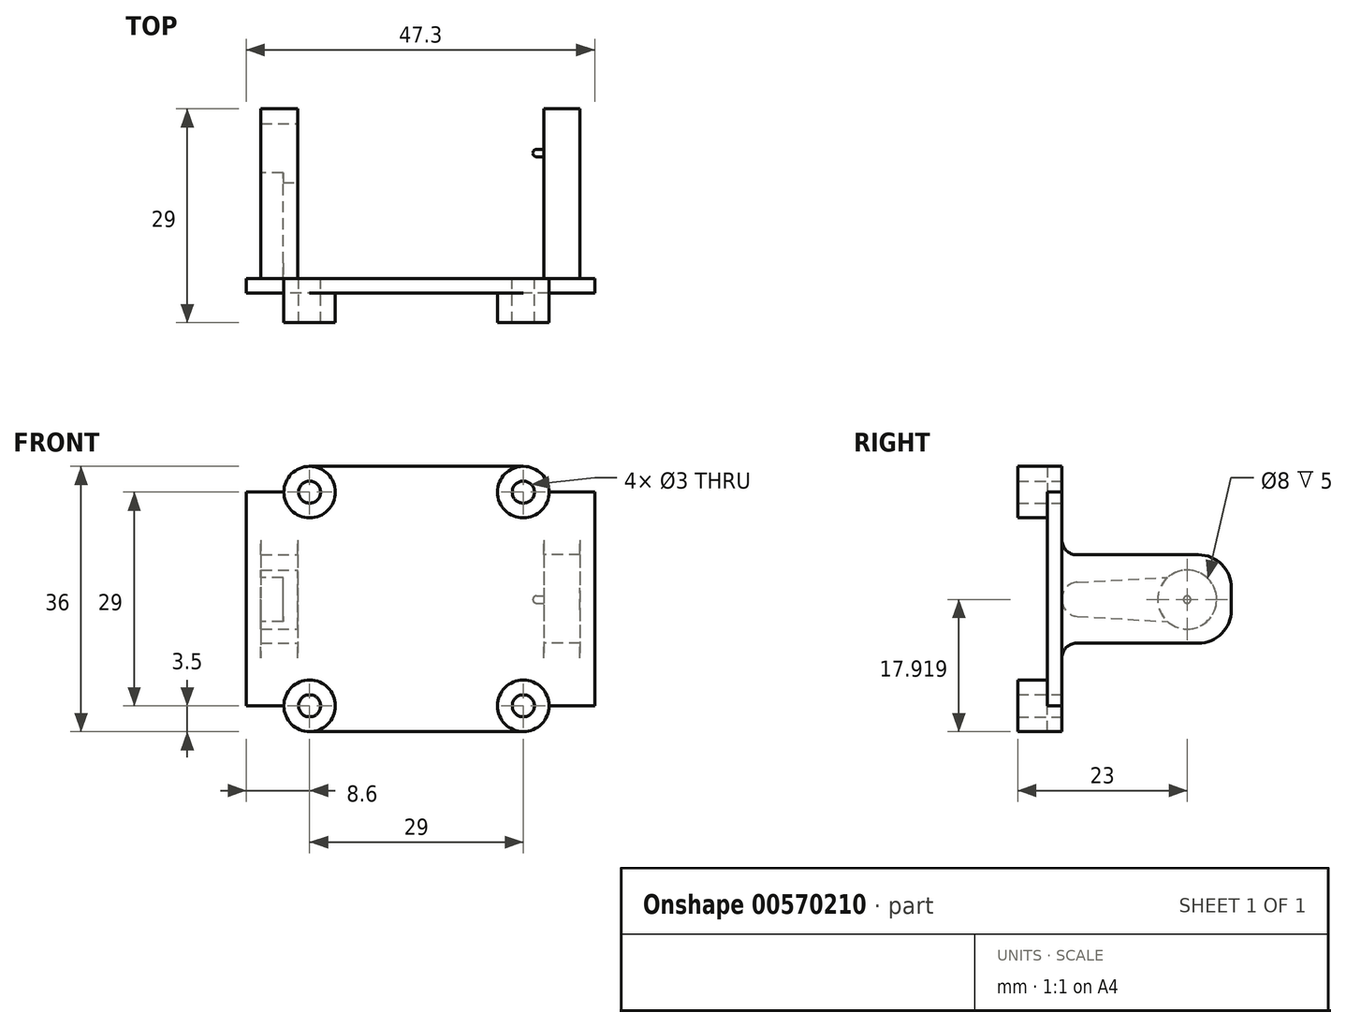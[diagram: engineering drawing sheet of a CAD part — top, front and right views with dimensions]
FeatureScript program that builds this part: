
annotation { "Feature Type Name" : "Feature", "Feature Type Description" : "" }
export const myFeature = defineFeature(function(context is Context, id is Id, definition is map)
    precondition{}
    {
        {
            var Q0;
            Q0=qCreatedBy(makeId("Front.planeOp"),FACE);
            var sketch = newSketch(context, id + "F0", { "sketchPlane" : qUnion([Q0])});
            skLineSegment(sketch, "E0.bottom", {"start": v(0, 0) * mm, "end": v(36, 0) * mm});
            skLineSegment(sketch, "E0.top", {"start": v(0, 36) * mm, "end": v(36, 36) * mm});
            skLineSegment(sketch, "E0.left", {"start": v(0, 0) * mm, "end": v(0, 36) * mm});
            skLineSegment(sketch, "E0.right", {"start": v(36, 0) * mm, "end": v(36, 36) * mm});
            skSolve(sketch);
        }
        {
            var Q0;
            Q0=makeQuery(id+"F0.imprint","IMPRINT",FACE,{"disambiguationData":[TD([[makeQuery(id+"F0.imprint","IMPRINT",EDGE,{"derivedFrom":sQuery(id+"F0.wireOp",EDGE,"E0.bottom")}),1.0]])]});
            extrude(context, id + "F1", {"entities" : qUnion([Q0]), "depth" : 2 * mm, "offsetDistance" : 25 * mm});
        }
        {
            var Q0;
            Q0=makeQuery(id+"F1.opExtrude","CAP_FACE",FACE,{"disambiguationData":[OSD([sQuery(id+"F0.wireOp",EDGE,"E0.bottom"),sQuery(id+"F0.wireOp",EDGE,"E0.top"),sQuery(id+"F0.wireOp",EDGE,"E0.left"),sQuery(id+"F0.wireOp",EDGE,"E0.right")])],"isStart":false});
            var sketch = newSketch(context, id + "F2", { "sketchPlane" : qUnion([Q0])});
            skCircle(sketch, "E1", {"center": v(3.5, 32.5) * mm, "radius": 3.5 * mm});
            skCircle(sketch, "E2", {"center": v(32.5, 32.5) * mm, "radius": 3.5 * mm});
            skCircle(sketch, "E3", {"center": v(32.5, 3.5) * mm, "radius": 3.5 * mm});
            skCircle(sketch, "E4", {"center": v(3.5, 3.5) * mm, "radius": 3.5 * mm});
            skCircle(sketch, "E5", {"center": v(3.5, 32.5) * mm, "radius": 1.5 * mm});
            skCircle(sketch, "E6", {"center": v(32.5, 32.5) * mm, "radius": 1.5 * mm});
            skCircle(sketch, "E7", {"center": v(32.5, 3.5) * mm, "radius": 1.5 * mm});
            skCircle(sketch, "E8", {"center": v(3.5, 3.5) * mm, "radius": 1.5 * mm});
            skSolve(sketch);
        }
        {
            var Q0;
            Q0=qSketchRegion(id+"F2",true);
            extrude(context, id + "F3", {"entities" : qUnion([Q0]), "operationType" : NewBodyOperationType.ADD, "depth" : 3 * mm, "offsetDistance" : 25 * mm});
        }
        {
            var Q0;
            Q0=makeQuery(id+"F1.opExtrude","SWEPT_EDGE",EDGE,{"disambiguationData":[OSD([sQuery(id+"F0.wireOp",EDGE,"E0.top"),sQuery(id+"F0.wireOp",EDGE,"E0.left")])]});
            var Q1;
            Q1=makeQuery(id+"F1.opExtrude","SWEPT_EDGE",EDGE,{"disambiguationData":[OSD([sQuery(id+"F0.wireOp",EDGE,"E0.top"),sQuery(id+"F0.wireOp",EDGE,"E0.right")])]});
            var Q2;
            Q2=makeQuery(id+"F1.opExtrude","SWEPT_EDGE",EDGE,{"disambiguationData":[OSD([sQuery(id+"F0.wireOp",EDGE,"E0.bottom"),sQuery(id+"F0.wireOp",EDGE,"E0.right")])]});
            var Q3;
            Q3=makeQuery(id+"F1.opExtrude","SWEPT_EDGE",EDGE,{"disambiguationData":[OSD([sQuery(id+"F0.wireOp",EDGE,"E0.bottom"),sQuery(id+"F0.wireOp",EDGE,"E0.left")])]});
            fillet(context, id + "F4", {"entities" : qUnion([Q0, Q1, Q2, Q3]), "radius" : 3.5 * mm, "tangentPropagation" : true, "allowEdgeOverflow" : false});
        }
        {
            var Q0;
            Q0=makeQuery(id+"F7.boolean.opBoolean","MERGE",FACE,{"derivedFrom":[makeQuery(id+"F1.opExtrude","SWEPT_FACE",FACE,{"disambiguationData":[OSD([sQuery(id+"F0.wireOp",EDGE,"E0.right")])]}),makeQuery(id+"F7.opExtrude","SWEPT_FACE",FACE,{"disambiguationData":[OSD([sQuery(id+"F6.wireOp",EDGE,"E11.left")])]})]});
            extrude(context, id + "F5", {"entities" : qUnion([Q0]), "operationType" : NewBodyOperationType.ADD, "depth" : 1.2 * mm, "offsetDistance" : 25 * mm});
        }
        {
            var Q0;
            Q0=makeQuery(id+"F1.opExtrude","CAP_FACE",FACE,{"disambiguationData":[OSD([sQuery(id+"F0.wireOp",EDGE,"E0.bottom"),sQuery(id+"F0.wireOp",EDGE,"E0.top"),sQuery(id+"F0.wireOp",EDGE,"E0.left"),sQuery(id+"F0.wireOp",EDGE,"E0.right")])],"isStart":true});
            var sketch = newSketch(context, id + "F6", { "sketchPlane" : qUnion([Q0])});
            skArc(sketch, "E9.0.1", {"start": v(0, 32.5) * mm, "mid": v(-1.03, 34.97) * mm, "end": v(-3.5, 36) * mm, "construction": true});
            skLineSegment(sketch, "E9.0.2", {"start": v(-3.5, 36) * mm, "end": v(-32.5, 36) * mm, "construction": true});
            skArc(sketch, "E9.0.3", {"start": v(-32.5, 36) * mm, "mid": v(-34.97, 34.97) * mm, "end": v(-36, 32.5) * mm, "construction": true});
            skArc(sketch, "E9.0.5", {"start": v(-36, 3.5) * mm, "mid": v(-34.97, 1.03) * mm, "end": v(-32.5, 0) * mm, "construction": true});
            skLineSegment(sketch, "E9.0.6", {"start": v(-32.5, 0) * mm, "end": v(-3.5, 0) * mm, "construction": true});
            skArc(sketch, "E9.0.7", {"start": v(-3.5, 0) * mm, "mid": v(-1.03, 1.03) * mm, "end": v(0, 3.5) * mm, "construction": true});
            skLineSegment(sketch, "E10.0", {"start": v(0, 3.5) * mm, "end": v(0, 32.5) * mm, "construction": true});
            skLineSegment(sketch, "E11.bottom", {"start": v(-37.2, 24) * mm, "end": v(-35.3, 24) * mm});
            skLineSegment(sketch, "E11.top", {"start": v(-37.2, 12) * mm, "end": v(-35.3, 12) * mm});
            skLineSegment(sketch, "E11.left", {"start": v(-37.2, 24) * mm, "end": v(-37.2, 12) * mm});
            skLineSegment(sketch, "E11.right", {"start": v(-35.3, 24) * mm, "end": v(-35.3, 12) * mm});
            skLineSegment(sketch, "E12.bottom", {"start": v(0, 24) * mm, "end": v(-1.9, 24) * mm});
            skLineSegment(sketch, "E12.top", {"start": v(0, 12) * mm, "end": v(-1.9, 12) * mm});
            skLineSegment(sketch, "E12.left", {"start": v(0, 24) * mm, "end": v(0, 12) * mm});
            skLineSegment(sketch, "E12.right", {"start": v(-1.9, 24) * mm, "end": v(-1.9, 12) * mm});
            skPoint(sketch, "E13", {"position": v(-1.9, 18) * mm});
            skPoint(sketch, "E14", {"position": v(0, 18) * mm});
            skLineSegment(sketch, "E15.0", {"start": v(-37.2, 3.5) * mm, "end": v(-37.2, 32.5) * mm, "construction": true});
            skSolve(sketch);
        }
        {
            var Q0;
            Q0=makeQuery(id+"F6.imprint","IMPRINT",FACE,{"disambiguationData":[TD([[makeQuery(id+"F6.imprint","IMPRINT",EDGE,{"derivedFrom":sQuery(id+"F6.wireOp",EDGE,"E11.bottom")}),-1.0]])]});
            var Q1;
            Q1=makeQuery(id+"F6.imprint","IMPRINT",FACE,{"disambiguationData":[TD([[makeQuery(id+"F6.imprint","IMPRINT",EDGE,{"derivedFrom":sQuery(id+"F6.wireOp",EDGE,"E12.bottom")}),1.0]])]});
            extrude(context, id + "F7", {"entities" : qUnion([Q0, Q1]), "operationType" : NewBodyOperationType.ADD, "depth" : 23 * mm, "offsetDistance" : 25 * mm});
        }
        {
            var Q0;
            Q0=makeQuery(id+"F7.boolean.opBoolean","MERGE",FACE,{"derivedFrom":[makeQuery(id+"F1.opExtrude","SWEPT_FACE",FACE,{"disambiguationData":[OSD([sQuery(id+"F0.wireOp",EDGE,"E0.left")])]}),makeQuery(id+"F7.opExtrude","SWEPT_FACE",FACE,{"disambiguationData":[OSD([sQuery(id+"F6.wireOp",EDGE,"E12.left")])]})]});
            extrude(context, id + "F8", {"entities" : qUnion([Q0]), "operationType" : NewBodyOperationType.ADD, "depth" : 1.2 * mm, "offsetDistance" : 25 * mm});
        }
        {
            var Q0;
            Q0=makeQuery(id+"F7.opExtrude","SWEPT_FACE",FACE,{"disambiguationData":[OSD([sQuery(id+"F6.wireOp",EDGE,"E12.right")])]});
            var sketch = newSketch(context, id + "F9", { "sketchPlane" : qUnion([Q0])});
            skCircle(sketch, "E16", {"center": v(17, 17.92) * mm, "radius": 4 * mm});
            skSolve(sketch);
        }
        {
            var Q0;
            Q0=makeQuery(id+"F7.opExtrude","SWEPT_FACE",FACE,{"disambiguationData":[OSD([sQuery(id+"F6.wireOp",EDGE,"E11.right")])]});
            var sketch = newSketch(context, id + "F10", { "sketchPlane" : qUnion([Q0])});
            skCircle(sketch, "E17.0", {"center": v(-17, 17.92) * mm, "radius": 4 * mm, "construction": true});
            skCircle(sketch, "E18", {"center": v(-17, 17.92) * mm, "radius": 0.5 * mm});
            skSolve(sketch);
        }
        {
            var Q0;
            Q0 = qSketchRegion(id + "F10", true);
            extrude(context, id + "F11", {"entities" : qUnion([Q0]), "operationType" : NewBodyOperationType.ADD, "depth" : 1.5 * mm, "offsetDistance" : 25 * mm});
        }
        {
            var Q0;
            Q0=makeQuery(id+"F11.opExtrude","CAP_EDGE",EDGE,{"disambiguationData":[OSD([sQuery(id+"F10.wireOp",EDGE,"E18")])],"isStart":false});
            fillet(context, id + "F12", {"entities" : qUnion([Q0]), "radius" : .5 * mm, "tangentPropagation" : true, "allowEdgeOverflow" : false});
        }
        {
            var Q0;
            Q0 = qSketchRegion(id + "F9", true);
            extrude(context, id + "F13", {"entities" : qUnion([Q0]), "operationType" : NewBodyOperationType.REMOVE, "oppositeDirection" : true, "depth" : 2.5 * mm, "offsetDistance" : 25 * mm});
        }
        {
            var Q0;
            Q0=makeQuery(id+"F7.opExtrude","CAP_EDGE",EDGE,{"disambiguationData":[OSD([sQuery(id+"F6.wireOp",EDGE,"E11.bottom")])],"isStart":false});
            var Q1;
            Q1=makeQuery(id+"F7.opExtrude","CAP_EDGE",EDGE,{"disambiguationData":[OSD([sQuery(id+"F6.wireOp",EDGE,"E11.top")])],"isStart":false});
            var Q2;
            {var subQ0=sQuery(id+"F6.wireOp",EDGE,"E12.left");var subQ1=sQuery(id+"F6.wireOp",EDGE,"E12.top");var subQ2=sQuery(id+"F0.wireOp",EDGE,"E0.left");Q2=makeQuery(id+"F8.boolean.opBoolean","MERGE",EDGE,{"derivedFrom":[makeQuery(id+"F7.opExtrude","CAP_EDGE",EDGE,{"disambiguationData":[OSD([subQ1])],"isStart":false}),makeQuery(id+"F8.opExtrude","SWEPT_EDGE",EDGE,{"disambiguationData":[OSD([subQ2,subQ1,subQ0]),TDD([makeQuery(id+"F7.opExtrude","CAP_VERTEX",VERTEX,{"disambiguationData":[OSD([subQ2,subQ1,subQ0])],"isStart":false})])]})]});}
            var Q3;
            {var subQ0=sQuery(id+"F6.wireOp",EDGE,"E12.left");var subQ1=sQuery(id+"F6.wireOp",EDGE,"E12.bottom");var subQ2=sQuery(id+"F0.wireOp",EDGE,"E0.left");Q3=makeQuery(id+"F8.boolean.opBoolean","MERGE",EDGE,{"derivedFrom":[makeQuery(id+"F7.opExtrude","CAP_EDGE",EDGE,{"disambiguationData":[OSD([subQ1])],"isStart":false}),makeQuery(id+"F8.opExtrude","SWEPT_EDGE",EDGE,{"disambiguationData":[OSD([subQ2,subQ1,subQ0]),TDD([makeQuery(id+"F7.opExtrude","CAP_VERTEX",VERTEX,{"disambiguationData":[OSD([subQ2,subQ1,subQ0])],"isStart":false})])]})]});}
            fillet(context, id + "F14", {"entities" : qUnion([Q0, Q1, Q2, Q3]), "radius" : 4.5 * mm, "tangentPropagation" : true, "allowEdgeOverflow" : false});
        }
        {
            var Q0;
            Q0=makeQuery(id+"F8.opExtrude","CAP_FACE",FACE,{"disambiguationData":[OSD([sQuery(id+"F0.wireOp",EDGE,"E0.left"),sQuery(id+"F6.wireOp",EDGE,"E12.left")])],"isStart":false});
            var sketch = newSketch(context, id + "F15", { "sketchPlane" : qUnion([Q0])});
            skCircle(sketch, "E19.0.0", {"center": v(-17, 17.92) * mm, "radius": 4 * mm});
            skLineSegment(sketch, "E20.left", {"start": v(-14.35, 20.92) * mm, "end": v(-14.35, 17.92) * mm});
            skLineSegment(sketch, "E20.right", {"start": v(0, 18.08) * mm, "end": v(0, 17.84) * mm});
            skLineSegment(sketch, "E21", {"start": v(-14.35, 20.92) * mm, "end": v(-2.08, 20.27) * mm});
            skLineSegment(sketch, "E22", {"start": v(-14.35, 14.92) * mm, "end": v(-2.07, 15.64) * mm});
            skPoint(sketch, "E23", {"position": v(-14.35, 17.92) * mm});
            skPoint(sketch, "E24", {"position": v(0, 17.92) * mm});
            skPoint(sketch, "E25.visualSharp", {"position": v(0, 20.17) * mm});
            skArc(sketch, "E25.filletArc", {"start": v(0, 18.08) * mm, "mid": v(-0.6, 19.6) * mm, "end": v(-2.08, 20.27) * mm});
            skPoint(sketch, "E26.visualSharp", {"position": v(0, 15.77) * mm});
            skArc(sketch, "E26.filletArc", {"start": v(-2.07, 15.64) * mm, "mid": v(-0.6, 16.33) * mm, "end": v(0, 17.84) * mm});
            skSolve(sketch);
        }
        {
            var Q0;
            Q0 = qSketchRegion(id + "F15", true);
            var Q1;
            Q1=makeQuery(id+"F7.opExtrude","SWEPT_FACE",FACE,{"disambiguationData":[OSD([sQuery(id+"F6.wireOp",EDGE,"E12.right")])]});
            extrude(context, id + "F16", {"entities" : qUnion([Q0]), "operationType" : NewBodyOperationType.REMOVE, "endBound" : BoundingType.UP_TO_SURFACE, "oppositeDirection" : true, "depth" : 25 * mm, "endBoundEntityFace" : qUnion([Q1]), "hasOffset" : true, "offsetDistance" : 2 * mm});
        }
        {
            var Q0;
            Q0=makeQuery(id+"F3.boolean.opBoolean","SPLIT",FACE,{"disambiguationData":[TD([makeQuery(id+"F3.opExtrude","SWEPT_FACE",FACE,{"disambiguationData":[OSD([sQuery(id+"F2.wireOp",EDGE,"E6")])]})])],"derivedFrom":makeQuery(id+"F1.opExtrude","CAP_FACE",FACE,{"disambiguationData":[OSD([sQuery(id+"F0.wireOp",EDGE,"E0.bottom"),sQuery(id+"F0.wireOp",EDGE,"E0.top"),sQuery(id+"F0.wireOp",EDGE,"E0.left"),sQuery(id+"F0.wireOp",EDGE,"E0.right")])],"isStart":false})});
            var Q1;
            Q1=makeQuery(id+"F3.boolean.opBoolean","SPLIT",FACE,{"disambiguationData":[TD([makeQuery(id+"F3.opExtrude","SWEPT_FACE",FACE,{"disambiguationData":[OSD([sQuery(id+"F2.wireOp",EDGE,"E7")])]})])],"derivedFrom":makeQuery(id+"F1.opExtrude","CAP_FACE",FACE,{"disambiguationData":[OSD([sQuery(id+"F0.wireOp",EDGE,"E0.bottom"),sQuery(id+"F0.wireOp",EDGE,"E0.top"),sQuery(id+"F0.wireOp",EDGE,"E0.left"),sQuery(id+"F0.wireOp",EDGE,"E0.right")])],"isStart":false})});
            var Q2;
            Q2=makeQuery(id+"F3.boolean.opBoolean","SPLIT",FACE,{"disambiguationData":[TD([makeQuery(id+"F3.opExtrude","SWEPT_FACE",FACE,{"disambiguationData":[OSD([sQuery(id+"F2.wireOp",EDGE,"E8")])]})])],"derivedFrom":makeQuery(id+"F1.opExtrude","CAP_FACE",FACE,{"disambiguationData":[OSD([sQuery(id+"F0.wireOp",EDGE,"E0.bottom"),sQuery(id+"F0.wireOp",EDGE,"E0.top"),sQuery(id+"F0.wireOp",EDGE,"E0.left"),sQuery(id+"F0.wireOp",EDGE,"E0.right")])],"isStart":false})});
            var Q3;
            Q3=makeQuery(id+"F3.boolean.opBoolean","SPLIT",FACE,{"disambiguationData":[TD([makeQuery(id+"F3.opExtrude","SWEPT_FACE",FACE,{"disambiguationData":[OSD([sQuery(id+"F2.wireOp",EDGE,"E5")])]})])],"derivedFrom":makeQuery(id+"F1.opExtrude","CAP_FACE",FACE,{"disambiguationData":[OSD([sQuery(id+"F0.wireOp",EDGE,"E0.bottom"),sQuery(id+"F0.wireOp",EDGE,"E0.top"),sQuery(id+"F0.wireOp",EDGE,"E0.left"),sQuery(id+"F0.wireOp",EDGE,"E0.right")])],"isStart":false})});
            extrude(context, id + "F17", {"entities" : qUnion([Q0, Q1, Q2, Q3]), "operationType" : NewBodyOperationType.REMOVE, "endBound" : BoundingType.UP_TO_NEXT, "oppositeDirection" : true, "depth" : 25 * mm, "offsetDistance" : 25 * mm});
        }
        {
            var Q0;
            Q0=makeQuery(id+"F7.boolean.opBoolean","MERGE",FACE,{"derivedFrom":[makeQuery(id+"F5.opExtrude","CAP_FACE",FACE,{"disambiguationData":[OSD([sQuery(id+"F0.wireOp",EDGE,"E0.right")])],"isStart":false}),makeQuery(id+"F7.opExtrude","SWEPT_FACE",FACE,{"disambiguationData":[OSD([sQuery(id+"F6.wireOp",EDGE,"E11.left")])]})]});
            extrude(context, id + "F18", {"entities" : qUnion([Q0]), "operationType" : NewBodyOperationType.ADD, "depth" : 3 * mm, "offsetDistance" : 25 * mm});
        }
        {
            var Q0;
            Q0=makeQuery(id+"F8.opExtrude","CAP_FACE",FACE,{"disambiguationData":[OSD([sQuery(id+"F0.wireOp",EDGE,"E0.left"),sQuery(id+"F6.wireOp",EDGE,"E12.left")])],"isStart":false});
            extrude(context, id + "F19", {"entities" : qUnion([Q0]), "operationType" : NewBodyOperationType.ADD, "depth" : 1.9 * mm, "offsetDistance" : 25 * mm});
        }
        {
            var Q0;
            Q0=makeQuery(id+"F18.opExtrude","CAP_FACE",FACE,{"disambiguationData":[OSD([sQuery(id+"F0.wireOp",EDGE,"E0.right"),sQuery(id+"F6.wireOp",EDGE,"E11.left")])],"isStart":false});
            var sketch = newSketch(context, id + "F20", { "sketchPlane" : qUnion([Q0])});
            skLineSegment(sketch, "E27.bottom", {"start": v(-2, 32.5) * mm, "end": v(0, 32.5) * mm});
            skLineSegment(sketch, "E27.top", {"start": v(-2, 3.5) * mm, "end": v(0, 3.5) * mm});
            skLineSegment(sketch, "E27.left", {"start": v(-2, 32.5) * mm, "end": v(-2, 3.5) * mm});
            skLineSegment(sketch, "E27.right", {"start": v(0, 32.5) * mm, "end": v(0, 3.5) * mm});
            skSolve(sketch);
        }
        {
            var Q0;
            Q0 = qSketchRegion(id + "F20", true);
            extrude(context, id + "F21", {"entities" : qUnion([Q0]), "operationType" : NewBodyOperationType.ADD, "depth" : 2 * mm, "offsetDistance" : 25 * mm});
        }
        {
            var Q0;
            Q0=makeQuery(id+"F19.opExtrude","CAP_FACE",FACE,{"disambiguationData":[OSD([sQuery(id+"F0.wireOp",EDGE,"E0.left"),sQuery(id+"F6.wireOp",EDGE,"E12.left")])],"isStart":false});
            var sketch = newSketch(context, id + "F22", { "sketchPlane" : qUnion([Q0])});
            skLineSegment(sketch, "E28.bottom", {"start": v(2, 32.5) * mm, "end": v(0, 32.5) * mm});
            skLineSegment(sketch, "E28.top", {"start": v(2, 3.5) * mm, "end": v(0, 3.5) * mm});
            skLineSegment(sketch, "E28.left", {"start": v(2, 32.5) * mm, "end": v(2, 3.5) * mm});
            skLineSegment(sketch, "E28.right", {"start": v(0, 32.5) * mm, "end": v(0, 3.5) * mm});
            skSolve(sketch);
        }
        {
            var Q0;
            Q0 = qSketchRegion(id + "F22", true);
            extrude(context, id + "F23", {"entities" : qUnion([Q0]), "operationType" : NewBodyOperationType.ADD, "depth" : 2 * mm, "offsetDistance" : 25 * mm});
        }
        {
            var Q0;
            {var subQ10=sQuery(id+"F22.wireOp",EDGE,"E28.right");var subQ12=sQuery(id+"F6.wireOp",EDGE,"E12.top");var subQ13=makeQuery(id+"F7.opExtrude","SWEPT_FACE",FACE,{"disambiguationData":[OSD([subQ12])]});Q0=makeQuery(id+"F23.boolean.opBoolean","SPLIT",EDGE,{"disambiguationData":[TD([subQ13])],"derivedFrom":makeQuery(id+"F23.opExtrude","CAP_EDGE",EDGE,{"disambiguationData":[OSD([subQ10])],"isStart":true})});}
            var Q1;
            {var subQ10=sQuery(id+"F22.wireOp",EDGE,"E28.right");var subQ17=sQuery(id+"F6.wireOp",EDGE,"E12.bottom");var subQ18=makeQuery(id+"F7.opExtrude","SWEPT_FACE",FACE,{"disambiguationData":[OSD([subQ17])]});Q1=makeQuery(id+"F23.boolean.opBoolean","SPLIT",EDGE,{"disambiguationData":[TD([subQ18])],"derivedFrom":makeQuery(id+"F23.opExtrude","CAP_EDGE",EDGE,{"disambiguationData":[OSD([subQ10])],"isStart":true})});}
            var Q2;
            Q2=makeQuery(id+"F7.opExtrude","CAP_EDGE",EDGE,{"disambiguationData":[OSD([sQuery(id+"F6.wireOp",EDGE,"E12.right")])],"isStart":true});
            var Q3;
            Q3=makeQuery(id+"F7.opExtrude","CAP_EDGE",EDGE,{"disambiguationData":[OSD([sQuery(id+"F6.wireOp",EDGE,"E11.right")])],"isStart":true});
            var Q4;
            Q4=makeQuery(id+"F21.opExtrude","CAP_EDGE",EDGE,{"disambiguationData":[OSD([sQuery(id+"F20.wireOp",EDGE,"E27.right")])],"isStart":true});
            var Q5;
            {var subQ0=sQuery(id+"F6.wireOp",EDGE,"E12.left");var subQ1=sQuery(id+"F6.wireOp",EDGE,"E12.top");var subQ2=sQuery(id+"F0.wireOp",EDGE,"E0.left");var subQ3=makeQuery(id+"F7.opExtrude","CAP_VERTEX",VERTEX,{"disambiguationData":[OSD([subQ2,subQ1,subQ0])],"isStart":true});Q5=makeQuery(id+"F19.boolean.opBoolean","MERGE",EDGE,{"derivedFrom":[makeQuery(id+"F8.boolean.opBoolean","MERGE",EDGE,{"derivedFrom":[makeQuery(id+"F7.opExtrude","CAP_EDGE",EDGE,{"disambiguationData":[OSD([subQ1])],"isStart":true}),makeQuery(id+"F8.opExtrude","SWEPT_EDGE",EDGE,{"disambiguationData":[OSD([subQ2,subQ1,subQ0]),TDD([subQ3])]})]}),makeQuery(id+"F19.opExtrude","SWEPT_EDGE",EDGE,{"disambiguationData":[OSD([subQ2,subQ1,subQ0]),TDD([makeQuery(id+"F8.opExtrude","CAP_VERTEX",VERTEX,{"disambiguationData":[OSD([subQ2,subQ1,subQ0]),TDD([subQ3])],"isStart":false})])]})]});}
            var Q6;
            {var subQ0=sQuery(id+"F6.wireOp",EDGE,"E12.left");var subQ1=sQuery(id+"F6.wireOp",EDGE,"E12.bottom");var subQ2=sQuery(id+"F0.wireOp",EDGE,"E0.left");var subQ3=makeQuery(id+"F7.opExtrude","CAP_VERTEX",VERTEX,{"disambiguationData":[OSD([subQ2,subQ1,subQ0])],"isStart":true});Q6=makeQuery(id+"F19.boolean.opBoolean","MERGE",EDGE,{"derivedFrom":[makeQuery(id+"F8.boolean.opBoolean","MERGE",EDGE,{"derivedFrom":[makeQuery(id+"F7.opExtrude","CAP_EDGE",EDGE,{"disambiguationData":[OSD([subQ1])],"isStart":true}),makeQuery(id+"F8.opExtrude","SWEPT_EDGE",EDGE,{"disambiguationData":[OSD([subQ2,subQ1,subQ0]),TDD([subQ3])]})]}),makeQuery(id+"F19.opExtrude","SWEPT_EDGE",EDGE,{"disambiguationData":[OSD([subQ2,subQ1,subQ0]),TDD([makeQuery(id+"F8.opExtrude","CAP_VERTEX",VERTEX,{"disambiguationData":[OSD([subQ2,subQ1,subQ0]),TDD([subQ3])],"isStart":false})])]})]});}
            var Q7;
            {var subQ0=sQuery(id+"F6.wireOp",EDGE,"E11.left");var subQ1=sQuery(id+"F6.wireOp",EDGE,"E11.bottom");var subQ2=sQuery(id+"F0.wireOp",EDGE,"E0.right");Q7=makeQuery(id+"F18.boolean.opBoolean","MERGE",EDGE,{"derivedFrom":[makeQuery(id+"F7.opExtrude","CAP_EDGE",EDGE,{"disambiguationData":[OSD([subQ1])],"isStart":true}),makeQuery(id+"F18.opExtrude","SWEPT_EDGE",EDGE,{"disambiguationData":[OSD([subQ2,subQ1,subQ0]),TDD([makeQuery(id+"F7.opExtrude","CAP_VERTEX",VERTEX,{"disambiguationData":[OSD([subQ2,subQ1,subQ0])],"isStart":true})])]})]});}
            var Q8;
            {var subQ0=sQuery(id+"F6.wireOp",EDGE,"E11.left");var subQ1=sQuery(id+"F6.wireOp",EDGE,"E11.top");var subQ2=sQuery(id+"F0.wireOp",EDGE,"E0.right");Q8=makeQuery(id+"F18.boolean.opBoolean","MERGE",EDGE,{"derivedFrom":[makeQuery(id+"F7.opExtrude","CAP_EDGE",EDGE,{"disambiguationData":[OSD([subQ1])],"isStart":true}),makeQuery(id+"F18.opExtrude","SWEPT_EDGE",EDGE,{"disambiguationData":[OSD([subQ2,subQ1,subQ0]),TDD([makeQuery(id+"F7.opExtrude","CAP_VERTEX",VERTEX,{"disambiguationData":[OSD([subQ2,subQ1,subQ0])],"isStart":true})])]})]});}
            fillet(context, id + "F24", {"entities" : qUnion([Q0, Q1, Q2, Q3, Q4, Q5, Q6, Q7, Q8]), "radius" : 2 * mm, "tangentPropagation" : true, "allowEdgeOverflow" : false});
        }
        {
            var Q0;
            Q0=makeQuery(id+"F3.opExtrude","CAP_FACE",FACE,{"disambiguationData":[OSD([sQuery(id+"F2.wireOp",EDGE,"E1"),sQuery(id+"F2.wireOp",EDGE,"E5")])],"isStart":false});
            var Q1;
            Q1=makeQuery(id+"F3.opExtrude","CAP_FACE",FACE,{"disambiguationData":[OSD([sQuery(id+"F2.wireOp",EDGE,"E2"),sQuery(id+"F2.wireOp",EDGE,"E6")])],"isStart":false});
            var Q2;
            Q2=makeQuery(id+"F3.opExtrude","CAP_FACE",FACE,{"disambiguationData":[OSD([sQuery(id+"F2.wireOp",EDGE,"E3"),sQuery(id+"F2.wireOp",EDGE,"E7")])],"isStart":false});
            var Q3;
            Q3=makeQuery(id+"F3.opExtrude","CAP_FACE",FACE,{"disambiguationData":[OSD([sQuery(id+"F2.wireOp",EDGE,"E4"),sQuery(id+"F2.wireOp",EDGE,"E8")])],"isStart":false});
            extrude(context, id + "F25", {"entities" : qUnion([Q0, Q1, Q2, Q3]), "operationType" : NewBodyOperationType.ADD, "depth" : 1 * mm, "offsetDistance" : 25 * mm});
        }
    });
